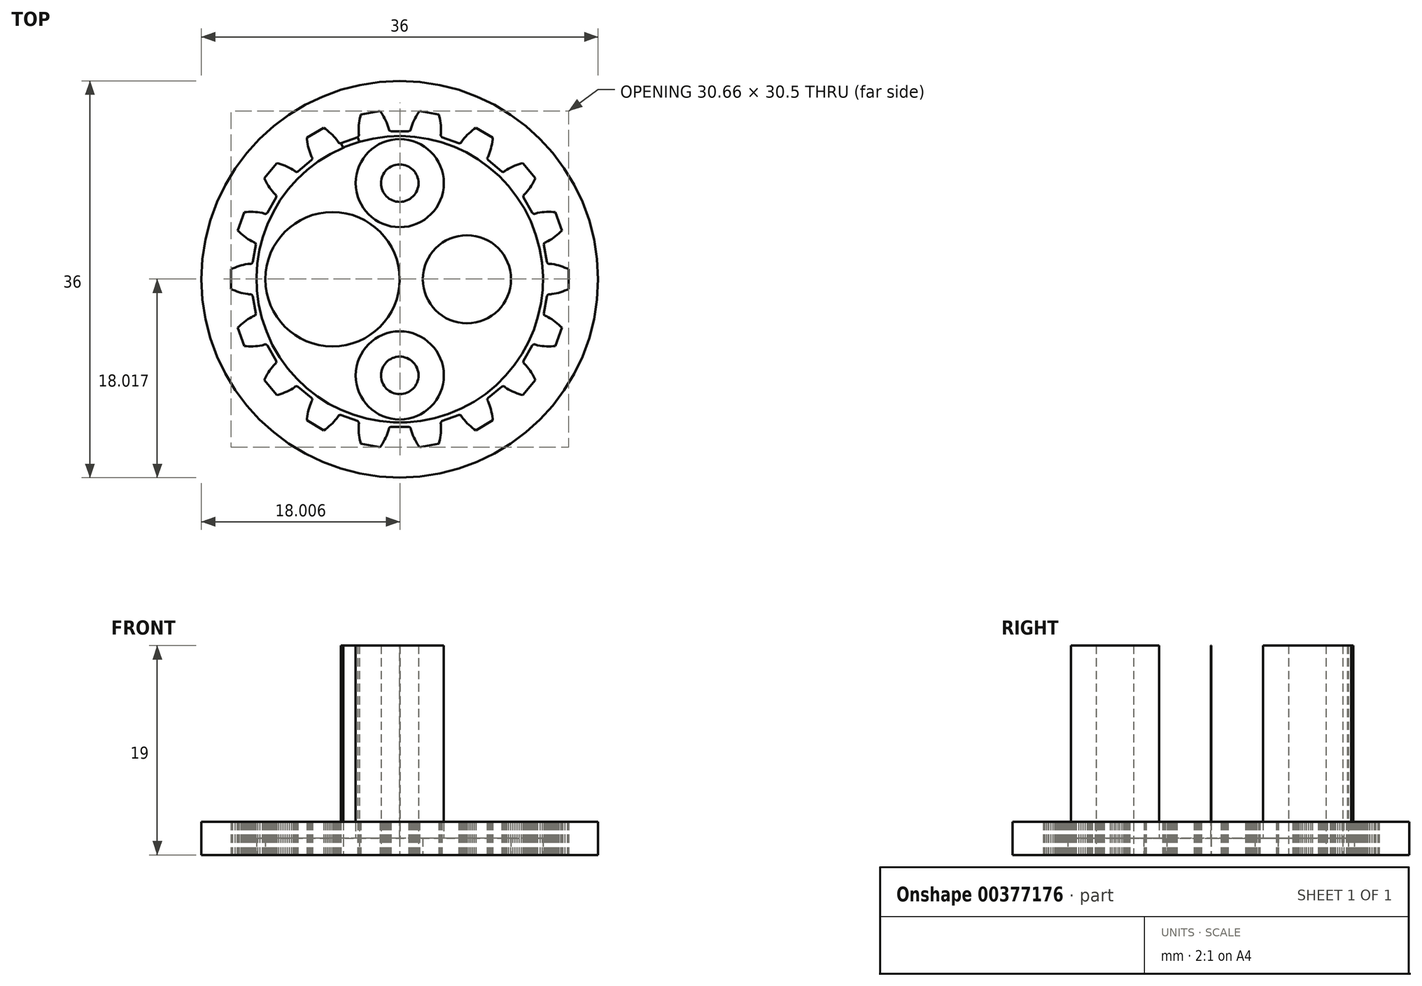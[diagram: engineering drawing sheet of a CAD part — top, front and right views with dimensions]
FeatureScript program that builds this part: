
annotation { "Feature Type Name" : "Feature", "Feature Type Description" : "" }
export const myFeature = defineFeature(function(context is Context, id is Id, definition is map)
    precondition{}
    {
        {
            var Q0;
            Q0=qCreatedBy(makeId("Top.planeOp"),FACE);
            var sketch = newSketch(context, id + "F0", { "sketchPlane" : qUnion([Q0])});
            skCircle(sketch, "E0", {"center": v(-6.1, 0) * mm, "radius": 6.1 * mm});
            skCircle(sketch, "E1.MirrorC", {"center": v(6.1, 0) * mm, "radius": 6.1 * mm});
            skCircle(sketch, "E2", {"center": v(0, 0) * mm, "radius": 18 * mm});
            skCircle(sketch, "E3", {"center": v(-6.1, 0) * mm, "radius": 4 * mm});
            skCircle(sketch, "E4", {"center": v(6.1, 0) * mm, "radius": 4 * mm});
            skCircle(sketch, "E5", {"center": v(0, -8.73) * mm, "radius": 4 * mm});
            skCircle(sketch, "E6", {"center": v(0, -8.73) * mm, "radius": 1.7 * mm});
            skCircle(sketch, "E7.cCircle", {"center": v(0, -8.73) * mm, "radius": 2.95 * mm, "construction": true});
            skLineSegment(sketch, "E7.0", {"start": v(0, -5.32) * mm, "end": v(2.95, -7.02) * mm});
            skLineSegment(sketch, "E7.1", {"start": v(2.95, -7.02) * mm, "end": v(2.95, -10.43) * mm});
            skLineSegment(sketch, "E7.2", {"start": v(2.95, -10.43) * mm, "end": v(0, -12.13) * mm});
            skLineSegment(sketch, "E7.3", {"start": v(0, -12.13) * mm, "end": v(-2.95, -10.43) * mm});
            skLineSegment(sketch, "E7.4", {"start": v(-2.95, -10.43) * mm, "end": v(-2.95, -7.02) * mm});
            skLineSegment(sketch, "E7.5", {"start": v(-2.95, -7.02) * mm, "end": v(0, -5.32) * mm});
            skLineSegment(sketch, "E8.MirrorCS", {"start": v(0, 12.13) * mm, "end": v(-2.95, 10.43) * mm});
            skLineSegment(sketch, "E9.MirrorCS", {"start": v(-2.95, 10.43) * mm, "end": v(-2.95, 7.02) * mm});
            skLineSegment(sketch, "E10.MirrorCS", {"start": v(-2.95, 7.02) * mm, "end": v(0, 5.32) * mm});
            skLineSegment(sketch, "E11.MirrorCS", {"start": v(2.95, 10.43) * mm, "end": v(0, 12.13) * mm});
            skCircle(sketch, "E12.MirrorC", {"center": v(0, 8.73) * mm, "radius": 1.7 * mm});
            skCircle(sketch, "E13.MirrorC", {"center": v(0, 8.73) * mm, "radius": 4 * mm});
            skLineSegment(sketch, "E14.MirrorCS", {"start": v(0, 5.32) * mm, "end": v(2.95, 7.02) * mm});
            skCircle(sketch, "E15.MirrorC", {"center": v(0, 8.73) * mm, "radius": 2.95 * mm, "construction": true});
            skLineSegment(sketch, "E16.MirrorCS", {"start": v(2.95, 7.02) * mm, "end": v(2.95, 10.43) * mm});
            skCircle(sketch, "E17", {"center": v(0, 0) * mm, "radius": 13 * mm});
            skLineSegment(sketch, "E18", {"start": v(13.36, 1.56) * mm, "end": v(13.42, 1.47) * mm});
            skLineSegment(sketch, "E19", {"start": v(13.42, 1.47) * mm, "end": v(13.48, 1.4) * mm});
            skLineSegment(sketch, "E20", {"start": v(13.48, 1.4) * mm, "end": v(13.52, 1.4) * mm});
            skLineSegment(sketch, "E21", {"start": v(13.52, 1.4) * mm, "end": v(13.62, 1.4) * mm});
            skLineSegment(sketch, "E22", {"start": v(13.62, 1.4) * mm, "end": v(13.72, 1.4) * mm});
            skLineSegment(sketch, "E23", {"start": v(13.72, 1.4) * mm, "end": v(13.81, 1.38) * mm});
            skLineSegment(sketch, "E24", {"start": v(13.81, 1.38) * mm, "end": v(14, 1.35) * mm});
            skLineSegment(sketch, "E25", {"start": v(14, 1.35) * mm, "end": v(14.2, 1.3) * mm});
            skLineSegment(sketch, "E26", {"start": v(14.2, 1.3) * mm, "end": v(14.4, 1.26) * mm});
            skLineSegment(sketch, "E27", {"start": v(14.4, 1.26) * mm, "end": v(14.6, 1.2) * mm});
            skLineSegment(sketch, "E28", {"start": v(14.6, 1.2) * mm, "end": v(14.8, 1.13) * mm});
            skLineSegment(sketch, "E29", {"start": v(14.8, 1.13) * mm, "end": v(15, 1.06) * mm});
            skLineSegment(sketch, "E30", {"start": v(15, 1.06) * mm, "end": v(15.19, 0.98) * mm});
            skLineSegment(sketch, "E31", {"start": v(15.19, 0.98) * mm, "end": v(15.33, 0.9) * mm});
            skLineSegment(sketch, "E32", {"start": v(15.33, 0.9) * mm, "end": v(15.33, -0.88) * mm});
            skLineSegment(sketch, "E33", {"start": v(15.33, -0.88) * mm, "end": v(15.19, -0.94) * mm});
            skLineSegment(sketch, "E34", {"start": v(15.19, -0.94) * mm, "end": v(15, -1.02) * mm});
            skLineSegment(sketch, "E35", {"start": v(15, -1.02) * mm, "end": v(14.8, -1.1) * mm});
            skLineSegment(sketch, "E36", {"start": v(14.8, -1.1) * mm, "end": v(14.6, -1.17) * mm});
            skLineSegment(sketch, "E37", {"start": v(14.6, -1.17) * mm, "end": v(14.4, -1.22) * mm});
            skLineSegment(sketch, "E38", {"start": v(14.4, -1.22) * mm, "end": v(14.2, -1.28) * mm});
            skLineSegment(sketch, "E39", {"start": v(14.2, -1.28) * mm, "end": v(14, -1.32) * mm});
            skLineSegment(sketch, "E40", {"start": v(14, -1.32) * mm, "end": v(13.81, -1.35) * mm});
            skLineSegment(sketch, "E41", {"start": v(13.81, -1.35) * mm, "end": v(13.72, -1.36) * mm});
            skLineSegment(sketch, "E42", {"start": v(13.72, -1.36) * mm, "end": v(13.62, -1.36) * mm});
            skLineSegment(sketch, "E43", {"start": v(13.62, -1.36) * mm, "end": v(13.52, -1.37) * mm});
            skLineSegment(sketch, "E44", {"start": v(13.52, -1.37) * mm, "end": v(13.48, -1.36) * mm});
            skLineSegment(sketch, "E45", {"start": v(13.48, -1.36) * mm, "end": v(13.42, -1.44) * mm});
            skLineSegment(sketch, "E46", {"start": v(13.42, -1.44) * mm, "end": v(13.36, -1.53) * mm});
            skLineSegment(sketch, "E47", {"start": v(13.36, -1.53) * mm, "end": v(13.08, -3.1) * mm});
            skLineSegment(sketch, "E48", {"start": v(13.08, -3.1) * mm, "end": v(13.1, -3.2) * mm});
            skLineSegment(sketch, "E49", {"start": v(13.1, -3.2) * mm, "end": v(13.14, -3.3) * mm});
            skLineSegment(sketch, "E50", {"start": v(13.14, -3.3) * mm, "end": v(13.18, -3.3) * mm});
            skLineSegment(sketch, "E51", {"start": v(13.18, -3.3) * mm, "end": v(13.27, -3.34) * mm});
            skLineSegment(sketch, "E52", {"start": v(13.27, -3.34) * mm, "end": v(13.36, -3.38) * mm});
            skLineSegment(sketch, "E53", {"start": v(13.36, -3.38) * mm, "end": v(13.45, -3.42) * mm});
            skLineSegment(sketch, "E54", {"start": v(13.45, -3.42) * mm, "end": v(13.62, -3.52) * mm});
            skLineSegment(sketch, "E55", {"start": v(13.62, -3.52) * mm, "end": v(13.79, -3.63) * mm});
            skLineSegment(sketch, "E56", {"start": v(13.79, -3.63) * mm, "end": v(13.96, -3.74) * mm});
            skLineSegment(sketch, "E57", {"start": v(13.96, -3.74) * mm, "end": v(14.12, -3.86) * mm});
            skLineSegment(sketch, "E58", {"start": v(14.12, -3.86) * mm, "end": v(14.28, -4) * mm});
            skLineSegment(sketch, "E59", {"start": v(14.28, -4) * mm, "end": v(14.44, -4.13) * mm});
            skLineSegment(sketch, "E60", {"start": v(14.44, -4.13) * mm, "end": v(14.6, -4.27) * mm});
            skLineSegment(sketch, "E61", {"start": v(14.6, -4.27) * mm, "end": v(14.72, -4.39) * mm});
            skLineSegment(sketch, "E62", {"start": v(14.72, -4.39) * mm, "end": v(14.1, -6.06) * mm});
            skLineSegment(sketch, "E63", {"start": v(14.1, -6.06) * mm, "end": v(13.94, -6.08) * mm});
            skLineSegment(sketch, "E64", {"start": v(13.94, -6.08) * mm, "end": v(13.73, -6.09) * mm});
            skLineSegment(sketch, "E65", {"start": v(13.73, -6.09) * mm, "end": v(13.52, -6.09) * mm});
            skLineSegment(sketch, "E66", {"start": v(13.52, -6.09) * mm, "end": v(13.31, -6.09) * mm});
            skLineSegment(sketch, "E67", {"start": v(13.31, -6.09) * mm, "end": v(13.1, -6.07) * mm});
            skLineSegment(sketch, "E68", {"start": v(13.1, -6.07) * mm, "end": v(12.9, -6.05) * mm});
            skLineSegment(sketch, "E69", {"start": v(12.9, -6.05) * mm, "end": v(12.7, -6.02) * mm});
            skLineSegment(sketch, "E70", {"start": v(12.7, -6.02) * mm, "end": v(12.51, -5.99) * mm});
            skLineSegment(sketch, "E71", {"start": v(12.51, -5.99) * mm, "end": v(12.42, -5.96) * mm});
            skLineSegment(sketch, "E72", {"start": v(12.42, -5.96) * mm, "end": v(12.33, -5.94) * mm});
            skLineSegment(sketch, "E73", {"start": v(12.33, -5.94) * mm, "end": v(12.24, -5.9) * mm});
            skLineSegment(sketch, "E74", {"start": v(12.24, -5.9) * mm, "end": v(12.2, -5.89) * mm});
            skLineSegment(sketch, "E75", {"start": v(12.2, -5.89) * mm, "end": v(12.11, -5.94) * mm});
            skLineSegment(sketch, "E76", {"start": v(12.11, -5.94) * mm, "end": v(12.03, -6) * mm});
            skLineSegment(sketch, "E77", {"start": v(12.03, -6) * mm, "end": v(11.23, -7.39) * mm});
            skLineSegment(sketch, "E78", {"start": v(11.23, -7.39) * mm, "end": v(11.22, -7.5) * mm});
            skLineSegment(sketch, "E79", {"start": v(11.22, -7.5) * mm, "end": v(11.21, -7.58) * mm});
            skLineSegment(sketch, "E80", {"start": v(11.21, -7.58) * mm, "end": v(11.25, -7.61) * mm});
            skLineSegment(sketch, "E81", {"start": v(11.25, -7.61) * mm, "end": v(11.32, -7.68) * mm});
            skLineSegment(sketch, "E82", {"start": v(11.32, -7.68) * mm, "end": v(11.4, -7.74) * mm});
            skLineSegment(sketch, "E83", {"start": v(11.4, -7.74) * mm, "end": v(11.46, -7.81) * mm});
            skLineSegment(sketch, "E84", {"start": v(11.46, -7.81) * mm, "end": v(11.59, -7.96) * mm});
            skLineSegment(sketch, "E85", {"start": v(11.59, -7.96) * mm, "end": v(11.71, -8.12) * mm});
            skLineSegment(sketch, "E86", {"start": v(11.71, -8.12) * mm, "end": v(11.83, -8.28) * mm});
            skLineSegment(sketch, "E87", {"start": v(11.83, -8.28) * mm, "end": v(11.94, -8.46) * mm});
            skLineSegment(sketch, "E88", {"start": v(11.94, -8.46) * mm, "end": v(12.05, -8.63) * mm});
            skLineSegment(sketch, "E89", {"start": v(12.05, -8.63) * mm, "end": v(12.15, -8.82) * mm});
            skLineSegment(sketch, "E90", {"start": v(12.15, -8.82) * mm, "end": v(12.25, -9) * mm});
            skLineSegment(sketch, "E91", {"start": v(12.25, -9) * mm, "end": v(12.32, -9.15) * mm});
            skLineSegment(sketch, "E92", {"start": v(12.32, -9.15) * mm, "end": v(11.17, -10.52) * mm});
            skLineSegment(sketch, "E93", {"start": v(11.17, -10.52) * mm, "end": v(11.02, -10.48) * mm});
            skLineSegment(sketch, "E94", {"start": v(11.02, -10.48) * mm, "end": v(10.82, -10.41) * mm});
            skLineSegment(sketch, "E95", {"start": v(10.82, -10.41) * mm, "end": v(10.62, -10.34) * mm});
            skLineSegment(sketch, "E96", {"start": v(10.62, -10.34) * mm, "end": v(10.42, -10.27) * mm});
            skLineSegment(sketch, "E97", {"start": v(10.42, -10.27) * mm, "end": v(10.23, -10.19) * mm});
            skLineSegment(sketch, "E98", {"start": v(10.23, -10.19) * mm, "end": v(10.05, -10.1) * mm});
            skLineSegment(sketch, "E99", {"start": v(10.05, -10.1) * mm, "end": v(9.88, -10) * mm});
            skLineSegment(sketch, "E100", {"start": v(9.88, -10) * mm, "end": v(9.7, -9.9) * mm});
            skLineSegment(sketch, "E101", {"start": v(9.7, -9.9) * mm, "end": v(9.63, -9.85) * mm});
            skLineSegment(sketch, "E102", {"start": v(9.63, -9.85) * mm, "end": v(9.55, -9.8) * mm});
            skLineSegment(sketch, "E103", {"start": v(9.55, -9.8) * mm, "end": v(9.47, -9.73) * mm});
            skLineSegment(sketch, "E104", {"start": v(9.47, -9.73) * mm, "end": v(9.44, -9.7) * mm});
            skLineSegment(sketch, "E105", {"start": v(9.44, -9.7) * mm, "end": v(9.35, -9.72) * mm});
            skLineSegment(sketch, "E106", {"start": v(9.35, -9.72) * mm, "end": v(9.25, -9.75) * mm});
            skLineSegment(sketch, "E107", {"start": v(9.25, -9.75) * mm, "end": v(8.02, -10.78) * mm});
            skLineSegment(sketch, "E108", {"start": v(8.02, -10.78) * mm, "end": v(7.97, -10.87) * mm});
            skLineSegment(sketch, "E109", {"start": v(7.97, -10.87) * mm, "end": v(7.94, -10.96) * mm});
            skLineSegment(sketch, "E110", {"start": v(7.94, -10.96) * mm, "end": v(7.96, -11) * mm});
            skLineSegment(sketch, "E111", {"start": v(7.96, -11) * mm, "end": v(8, -11.08) * mm});
            skLineSegment(sketch, "E112", {"start": v(8, -11.08) * mm, "end": v(8.05, -11.17) * mm});
            skLineSegment(sketch, "E113", {"start": v(8.05, -11.17) * mm, "end": v(8.1, -11.26) * mm});
            skLineSegment(sketch, "E114", {"start": v(8.1, -11.26) * mm, "end": v(8.16, -11.44) * mm});
            skLineSegment(sketch, "E115", {"start": v(8.16, -11.44) * mm, "end": v(8.22, -11.63) * mm});
            skLineSegment(sketch, "E116", {"start": v(8.22, -11.63) * mm, "end": v(8.28, -11.83) * mm});
            skLineSegment(sketch, "E117", {"start": v(8.28, -11.83) * mm, "end": v(8.33, -12.03) * mm});
            skLineSegment(sketch, "E118", {"start": v(8.33, -12.03) * mm, "end": v(8.37, -12.23) * mm});
            skLineSegment(sketch, "E119", {"start": v(8.37, -12.23) * mm, "end": v(8.4, -12.44) * mm});
            skLineSegment(sketch, "E120", {"start": v(8.4, -12.44) * mm, "end": v(8.43, -12.65) * mm});
            skLineSegment(sketch, "E121", {"start": v(8.43, -12.65) * mm, "end": v(8.44, -12.81) * mm});
            skLineSegment(sketch, "E122", {"start": v(8.44, -12.81) * mm, "end": v(6.9, -13.7) * mm});
            skLineSegment(sketch, "E123", {"start": v(6.9, -13.7) * mm, "end": v(6.77, -13.6) * mm});
            skLineSegment(sketch, "E124", {"start": v(6.77, -13.6) * mm, "end": v(6.6, -13.48) * mm});
            skLineSegment(sketch, "E125", {"start": v(6.6, -13.48) * mm, "end": v(6.43, -13.35) * mm});
            skLineSegment(sketch, "E126", {"start": v(6.43, -13.35) * mm, "end": v(6.28, -13.21) * mm});
            skLineSegment(sketch, "E127", {"start": v(6.28, -13.21) * mm, "end": v(6.13, -13.07) * mm});
            skLineSegment(sketch, "E128", {"start": v(6.13, -13.07) * mm, "end": v(5.99, -12.93) * mm});
            skLineSegment(sketch, "E129", {"start": v(5.99, -12.93) * mm, "end": v(5.85, -12.78) * mm});
            skLineSegment(sketch, "E130", {"start": v(5.85, -12.78) * mm, "end": v(5.73, -12.62) * mm});
            skLineSegment(sketch, "E131", {"start": v(5.73, -12.62) * mm, "end": v(5.67, -12.54) * mm});
            skLineSegment(sketch, "E132", {"start": v(5.67, -12.54) * mm, "end": v(5.62, -12.46) * mm});
            skLineSegment(sketch, "E133", {"start": v(5.62, -12.46) * mm, "end": v(5.57, -12.38) * mm});
            skLineSegment(sketch, "E134", {"start": v(5.57, -12.38) * mm, "end": v(5.55, -12.34) * mm});
            skLineSegment(sketch, "E135", {"start": v(5.55, -12.34) * mm, "end": v(5.45, -12.33) * mm});
            skLineSegment(sketch, "E136", {"start": v(5.45, -12.33) * mm, "end": v(5.35, -12.32) * mm});
            skLineSegment(sketch, "E137", {"start": v(5.35, -12.32) * mm, "end": v(3.84, -12.87) * mm});
            skLineSegment(sketch, "E138", {"start": v(3.84, -12.87) * mm, "end": v(3.77, -12.94) * mm});
            skLineSegment(sketch, "E139", {"start": v(3.77, -12.94) * mm, "end": v(3.7, -13) * mm});
            skLineSegment(sketch, "E140", {"start": v(3.7, -13) * mm, "end": v(3.71, -13.06) * mm});
            skLineSegment(sketch, "E141", {"start": v(3.71, -13.06) * mm, "end": v(3.73, -13.15) * mm});
            skLineSegment(sketch, "E142", {"start": v(3.73, -13.15) * mm, "end": v(3.74, -13.25) * mm});
            skLineSegment(sketch, "E143", {"start": v(3.74, -13.25) * mm, "end": v(3.75, -13.34) * mm});
            skLineSegment(sketch, "E144", {"start": v(3.75, -13.34) * mm, "end": v(3.75, -13.54) * mm});
            skLineSegment(sketch, "E145", {"start": v(3.75, -13.54) * mm, "end": v(3.74, -13.74) * mm});
            skLineSegment(sketch, "E146", {"start": v(3.74, -13.74) * mm, "end": v(3.73, -13.94) * mm});
            skLineSegment(sketch, "E147", {"start": v(3.73, -13.94) * mm, "end": v(3.7, -14.15) * mm});
            skLineSegment(sketch, "E148", {"start": v(3.7, -14.15) * mm, "end": v(3.67, -14.35) * mm});
            skLineSegment(sketch, "E149", {"start": v(3.67, -14.35) * mm, "end": v(3.63, -14.56) * mm});
            skLineSegment(sketch, "E150", {"start": v(3.63, -14.56) * mm, "end": v(3.59, -14.77) * mm});
            skLineSegment(sketch, "E151", {"start": v(3.59, -14.77) * mm, "end": v(3.55, -14.92) * mm});
            skLineSegment(sketch, "E152", {"start": v(3.55, -14.92) * mm, "end": v(1.79, -15.23) * mm});
            skLineSegment(sketch, "E153", {"start": v(1.79, -15.23) * mm, "end": v(1.7, -15.1) * mm});
            skLineSegment(sketch, "E154", {"start": v(1.7, -15.1) * mm, "end": v(1.58, -14.92) * mm});
            skLineSegment(sketch, "E155", {"start": v(1.58, -14.92) * mm, "end": v(1.48, -14.74) * mm});
            skLineSegment(sketch, "E156", {"start": v(1.48, -14.74) * mm, "end": v(1.37, -14.56) * mm});
            skLineSegment(sketch, "E157", {"start": v(1.37, -14.56) * mm, "end": v(1.28, -14.37) * mm});
            skLineSegment(sketch, "E158", {"start": v(1.28, -14.37) * mm, "end": v(1.2, -14.2) * mm});
            skLineSegment(sketch, "E159", {"start": v(1.2, -14.2) * mm, "end": v(1.12, -14) * mm});
            skLineSegment(sketch, "E160", {"start": v(1.12, -14) * mm, "end": v(1.06, -13.82) * mm});
            skLineSegment(sketch, "E161", {"start": v(1.06, -13.82) * mm, "end": v(1.03, -13.72) * mm});
            skLineSegment(sketch, "E162", {"start": v(1.03, -13.72) * mm, "end": v(1.01, -13.63) * mm});
            skLineSegment(sketch, "E163", {"start": v(1.01, -13.63) * mm, "end": v(1, -13.54) * mm});
            skLineSegment(sketch, "E164", {"start": v(1, -13.54) * mm, "end": v(0.99, -13.49) * mm});
            skLineSegment(sketch, "E165", {"start": v(0.99, -13.49) * mm, "end": v(0.9, -13.45) * mm});
            skLineSegment(sketch, "E166", {"start": v(0.9, -13.45) * mm, "end": v(0.8, -13.4) * mm});
            skLineSegment(sketch, "E167", {"start": v(0.8, -13.4) * mm, "end": v(-0.8, -13.4) * mm});
            skLineSegment(sketch, "E168", {"start": v(-0.8, -13.4) * mm, "end": v(-0.9, -13.45) * mm});
            skLineSegment(sketch, "E169", {"start": v(-0.9, -13.45) * mm, "end": v(-0.97, -13.49) * mm});
            skLineSegment(sketch, "E170", {"start": v(-0.97, -13.49) * mm, "end": v(-0.98, -13.54) * mm});
            skLineSegment(sketch, "E171", {"start": v(-0.98, -13.54) * mm, "end": v(-1, -13.63) * mm});
            skLineSegment(sketch, "E172", {"start": v(-1, -13.63) * mm, "end": v(-1.02, -13.72) * mm});
            skLineSegment(sketch, "E173", {"start": v(-1.02, -13.72) * mm, "end": v(-1.05, -13.82) * mm});
            skLineSegment(sketch, "E174", {"start": v(-1.05, -13.82) * mm, "end": v(-1.11, -14) * mm});
            skLineSegment(sketch, "E175", {"start": v(-1.11, -14) * mm, "end": v(-1.19, -14.2) * mm});
            skLineSegment(sketch, "E176", {"start": v(-1.19, -14.2) * mm, "end": v(-1.27, -14.37) * mm});
            skLineSegment(sketch, "E177", {"start": v(-1.27, -14.37) * mm, "end": v(-1.36, -14.56) * mm});
            skLineSegment(sketch, "E178", {"start": v(-1.36, -14.56) * mm, "end": v(-1.46, -14.74) * mm});
            skLineSegment(sketch, "E179", {"start": v(-1.46, -14.74) * mm, "end": v(-1.57, -14.92) * mm});
            skLineSegment(sketch, "E180", {"start": v(-1.57, -14.92) * mm, "end": v(-1.69, -15.1) * mm});
            skLineSegment(sketch, "E181", {"start": v(-1.69, -15.1) * mm, "end": v(-1.78, -15.23) * mm});
            skLineSegment(sketch, "E182", {"start": v(-1.78, -15.23) * mm, "end": v(-3.53, -14.92) * mm});
            skLineSegment(sketch, "E183", {"start": v(-3.53, -14.92) * mm, "end": v(-3.57, -14.77) * mm});
            skLineSegment(sketch, "E184", {"start": v(-3.57, -14.77) * mm, "end": v(-3.62, -14.56) * mm});
            skLineSegment(sketch, "E185", {"start": v(-3.62, -14.56) * mm, "end": v(-3.66, -14.35) * mm});
            skLineSegment(sketch, "E186", {"start": v(-3.66, -14.35) * mm, "end": v(-3.7, -14.15) * mm});
            skLineSegment(sketch, "E187", {"start": v(-3.7, -14.15) * mm, "end": v(-3.72, -13.94) * mm});
            skLineSegment(sketch, "E188", {"start": v(-3.72, -13.94) * mm, "end": v(-3.73, -13.74) * mm});
            skLineSegment(sketch, "E189", {"start": v(-3.73, -13.74) * mm, "end": v(-3.74, -13.54) * mm});
            skLineSegment(sketch, "E190", {"start": v(-3.74, -13.54) * mm, "end": v(-3.73, -13.34) * mm});
            skLineSegment(sketch, "E191", {"start": v(-3.73, -13.34) * mm, "end": v(-3.73, -13.25) * mm});
            skLineSegment(sketch, "E192", {"start": v(-3.73, -13.25) * mm, "end": v(-3.72, -13.15) * mm});
            skLineSegment(sketch, "E193", {"start": v(-3.72, -13.15) * mm, "end": v(-3.7, -13.06) * mm});
            skLineSegment(sketch, "E194", {"start": v(-3.7, -13.06) * mm, "end": v(-3.7, -13) * mm});
            skLineSegment(sketch, "E195", {"start": v(-3.7, -13) * mm, "end": v(-3.76, -12.94) * mm});
            skLineSegment(sketch, "E196", {"start": v(-3.76, -12.94) * mm, "end": v(-3.83, -12.87) * mm});
            skLineSegment(sketch, "E197", {"start": v(-3.83, -12.87) * mm, "end": v(-5.34, -12.32) * mm});
            skLineSegment(sketch, "E198", {"start": v(-5.34, -12.32) * mm, "end": v(-5.44, -12.33) * mm});
            skLineSegment(sketch, "E199", {"start": v(-5.44, -12.33) * mm, "end": v(-5.53, -12.34) * mm});
            skLineSegment(sketch, "E200", {"start": v(-5.53, -12.34) * mm, "end": v(-5.56, -12.38) * mm});
            skLineSegment(sketch, "E201", {"start": v(-5.56, -12.38) * mm, "end": v(-5.6, -12.46) * mm});
            skLineSegment(sketch, "E202", {"start": v(-5.6, -12.46) * mm, "end": v(-5.66, -12.54) * mm});
            skLineSegment(sketch, "E203", {"start": v(-5.66, -12.54) * mm, "end": v(-5.72, -12.62) * mm});
            skLineSegment(sketch, "E204", {"start": v(-5.72, -12.62) * mm, "end": v(-5.84, -12.78) * mm});
            skLineSegment(sketch, "E205", {"start": v(-5.84, -12.78) * mm, "end": v(-5.97, -12.93) * mm});
            skLineSegment(sketch, "E206", {"start": v(-5.97, -12.93) * mm, "end": v(-6.12, -13.07) * mm});
            skLineSegment(sketch, "E207", {"start": v(-6.12, -13.07) * mm, "end": v(-6.27, -13.21) * mm});
            skLineSegment(sketch, "E208", {"start": v(-6.27, -13.21) * mm, "end": v(-6.42, -13.35) * mm});
            skLineSegment(sketch, "E209", {"start": v(-6.42, -13.35) * mm, "end": v(-6.59, -13.48) * mm});
            skLineSegment(sketch, "E210", {"start": v(-6.59, -13.48) * mm, "end": v(-6.75, -13.6) * mm});
            skLineSegment(sketch, "E211", {"start": v(-6.75, -13.6) * mm, "end": v(-6.89, -13.7) * mm});
            skLineSegment(sketch, "E212", {"start": v(-6.89, -13.7) * mm, "end": v(-8.43, -12.81) * mm});
            skLineSegment(sketch, "E213", {"start": v(-8.43, -12.81) * mm, "end": v(-8.41, -12.65) * mm});
            skLineSegment(sketch, "E214", {"start": v(-8.41, -12.65) * mm, "end": v(-8.39, -12.44) * mm});
            skLineSegment(sketch, "E215", {"start": v(-8.39, -12.44) * mm, "end": v(-8.35, -12.23) * mm});
            skLineSegment(sketch, "E216", {"start": v(-8.35, -12.23) * mm, "end": v(-8.31, -12.03) * mm});
            skLineSegment(sketch, "E217", {"start": v(-8.31, -12.03) * mm, "end": v(-8.27, -11.83) * mm});
            skLineSegment(sketch, "E218", {"start": v(-8.27, -11.83) * mm, "end": v(-8.21, -11.63) * mm});
            skLineSegment(sketch, "E219", {"start": v(-8.21, -11.63) * mm, "end": v(-8.15, -11.44) * mm});
            skLineSegment(sketch, "E220", {"start": v(-8.15, -11.44) * mm, "end": v(-8.08, -11.26) * mm});
            skLineSegment(sketch, "E221", {"start": v(-8.08, -11.26) * mm, "end": v(-8.04, -11.17) * mm});
            skLineSegment(sketch, "E222", {"start": v(-8.04, -11.17) * mm, "end": v(-8, -11.08) * mm});
            skLineSegment(sketch, "E223", {"start": v(-8, -11.08) * mm, "end": v(-7.95, -11) * mm});
            skLineSegment(sketch, "E224", {"start": v(-7.95, -11) * mm, "end": v(-7.93, -10.96) * mm});
            skLineSegment(sketch, "E225", {"start": v(-7.93, -10.96) * mm, "end": v(-7.96, -10.87) * mm});
            skLineSegment(sketch, "E226", {"start": v(-7.96, -10.87) * mm, "end": v(-8, -10.78) * mm});
            skLineSegment(sketch, "E227", {"start": v(-8, -10.78) * mm, "end": v(-9.24, -9.75) * mm});
            skLineSegment(sketch, "E228", {"start": v(-9.24, -9.75) * mm, "end": v(-9.33, -9.72) * mm});
            skLineSegment(sketch, "E229", {"start": v(-9.33, -9.72) * mm, "end": v(-9.43, -9.7) * mm});
            skLineSegment(sketch, "E230", {"start": v(-9.43, -9.7) * mm, "end": v(-9.46, -9.73) * mm});
            skLineSegment(sketch, "E231", {"start": v(-9.46, -9.73) * mm, "end": v(-9.54, -9.8) * mm});
            skLineSegment(sketch, "E232", {"start": v(-9.54, -9.8) * mm, "end": v(-9.61, -9.85) * mm});
            skLineSegment(sketch, "E233", {"start": v(-9.61, -9.85) * mm, "end": v(-9.7, -9.9) * mm});
            skLineSegment(sketch, "E234", {"start": v(-9.7, -9.9) * mm, "end": v(-9.86, -10) * mm});
            skLineSegment(sketch, "E235", {"start": v(-9.86, -10) * mm, "end": v(-10.04, -10.1) * mm});
            skLineSegment(sketch, "E236", {"start": v(-10.04, -10.1) * mm, "end": v(-10.22, -10.19) * mm});
            skLineSegment(sketch, "E237", {"start": v(-10.22, -10.19) * mm, "end": v(-10.41, -10.27) * mm});
            skLineSegment(sketch, "E238", {"start": v(-10.41, -10.27) * mm, "end": v(-10.6, -10.34) * mm});
            skLineSegment(sketch, "E239", {"start": v(-10.6, -10.34) * mm, "end": v(-10.8, -10.41) * mm});
            skLineSegment(sketch, "E240", {"start": v(-10.8, -10.41) * mm, "end": v(-11, -10.48) * mm});
            skLineSegment(sketch, "E241", {"start": v(-11, -10.48) * mm, "end": v(-11.16, -10.52) * mm});
            skLineSegment(sketch, "E242", {"start": v(-11.16, -10.52) * mm, "end": v(-12.31, -9.15) * mm});
            skLineSegment(sketch, "E243", {"start": v(-12.31, -9.15) * mm, "end": v(-12.24, -9) * mm});
            skLineSegment(sketch, "E244", {"start": v(-12.24, -9) * mm, "end": v(-12.14, -8.82) * mm});
            skLineSegment(sketch, "E245", {"start": v(-12.14, -8.82) * mm, "end": v(-12.04, -8.63) * mm});
            skLineSegment(sketch, "E246", {"start": v(-12.04, -8.63) * mm, "end": v(-11.93, -8.46) * mm});
            skLineSegment(sketch, "E247", {"start": v(-11.93, -8.46) * mm, "end": v(-11.82, -8.28) * mm});
            skLineSegment(sketch, "E248", {"start": v(-11.82, -8.28) * mm, "end": v(-11.7, -8.12) * mm});
            skLineSegment(sketch, "E249", {"start": v(-11.7, -8.12) * mm, "end": v(-11.58, -7.96) * mm});
            skLineSegment(sketch, "E250", {"start": v(-11.58, -7.96) * mm, "end": v(-11.45, -7.81) * mm});
            skLineSegment(sketch, "E251", {"start": v(-11.45, -7.81) * mm, "end": v(-11.38, -7.74) * mm});
            skLineSegment(sketch, "E252", {"start": v(-11.38, -7.74) * mm, "end": v(-11.31, -7.68) * mm});
            skLineSegment(sketch, "E253", {"start": v(-11.31, -7.68) * mm, "end": v(-11.24, -7.61) * mm});
            skLineSegment(sketch, "E254", {"start": v(-11.24, -7.61) * mm, "end": v(-11.2, -7.58) * mm});
            skLineSegment(sketch, "E255", {"start": v(-11.2, -7.58) * mm, "end": v(-11.2, -7.5) * mm});
            skLineSegment(sketch, "E256", {"start": v(-11.2, -7.5) * mm, "end": v(-11.22, -7.39) * mm});
            skLineSegment(sketch, "E257", {"start": v(-11.22, -7.39) * mm, "end": v(-12.02, -6) * mm});
            skLineSegment(sketch, "E258", {"start": v(-12.02, -6) * mm, "end": v(-12.1, -5.94) * mm});
            skLineSegment(sketch, "E259", {"start": v(-12.1, -5.94) * mm, "end": v(-12.18, -5.89) * mm});
            skLineSegment(sketch, "E260", {"start": v(-12.18, -5.89) * mm, "end": v(-12.22, -5.9) * mm});
            skLineSegment(sketch, "E261", {"start": v(-12.22, -5.9) * mm, "end": v(-12.32, -5.94) * mm});
            skLineSegment(sketch, "E262", {"start": v(-12.32, -5.94) * mm, "end": v(-12.4, -5.96) * mm});
            skLineSegment(sketch, "E263", {"start": v(-12.4, -5.96) * mm, "end": v(-12.5, -5.99) * mm});
            skLineSegment(sketch, "E264", {"start": v(-12.5, -5.99) * mm, "end": v(-12.7, -6.02) * mm});
            skLineSegment(sketch, "E265", {"start": v(-12.7, -6.02) * mm, "end": v(-12.9, -6.05) * mm});
            skLineSegment(sketch, "E266", {"start": v(-12.9, -6.05) * mm, "end": v(-13.1, -6.07) * mm});
            skLineSegment(sketch, "E267", {"start": v(-13.1, -6.07) * mm, "end": v(-13.3, -6.09) * mm});
            skLineSegment(sketch, "E268", {"start": v(-13.3, -6.09) * mm, "end": v(-13.5, -6.09) * mm});
            skLineSegment(sketch, "E269", {"start": v(-13.5, -6.09) * mm, "end": v(-13.72, -6.09) * mm});
            skLineSegment(sketch, "E270", {"start": v(-13.72, -6.09) * mm, "end": v(-13.93, -6.08) * mm});
            skLineSegment(sketch, "E271", {"start": v(-13.93, -6.08) * mm, "end": v(-14.1, -6.06) * mm});
            skLineSegment(sketch, "E272", {"start": v(-14.1, -6.06) * mm, "end": v(-14.7, -4.39) * mm});
            skLineSegment(sketch, "E273", {"start": v(-14.7, -4.39) * mm, "end": v(-14.59, -4.27) * mm});
            skLineSegment(sketch, "E274", {"start": v(-14.59, -4.27) * mm, "end": v(-14.43, -4.13) * mm});
            skLineSegment(sketch, "E275", {"start": v(-14.43, -4.13) * mm, "end": v(-14.27, -4) * mm});
            skLineSegment(sketch, "E276", {"start": v(-14.27, -4) * mm, "end": v(-14.1, -3.86) * mm});
            skLineSegment(sketch, "E277", {"start": v(-14.1, -3.86) * mm, "end": v(-13.95, -3.74) * mm});
            skLineSegment(sketch, "E278", {"start": v(-13.95, -3.74) * mm, "end": v(-13.78, -3.63) * mm});
            skLineSegment(sketch, "E279", {"start": v(-13.78, -3.63) * mm, "end": v(-13.6, -3.52) * mm});
            skLineSegment(sketch, "E280", {"start": v(-13.6, -3.52) * mm, "end": v(-13.44, -3.42) * mm});
            skLineSegment(sketch, "E281", {"start": v(-13.44, -3.42) * mm, "end": v(-13.35, -3.38) * mm});
            skLineSegment(sketch, "E282", {"start": v(-13.35, -3.38) * mm, "end": v(-13.26, -3.34) * mm});
            skLineSegment(sketch, "E283", {"start": v(-13.26, -3.34) * mm, "end": v(-13.17, -3.3) * mm});
            skLineSegment(sketch, "E284", {"start": v(-13.17, -3.3) * mm, "end": v(-13.12, -3.3) * mm});
            skLineSegment(sketch, "E285", {"start": v(-13.12, -3.3) * mm, "end": v(-13.1, -3.2) * mm});
            skLineSegment(sketch, "E286", {"start": v(-13.1, -3.2) * mm, "end": v(-13.07, -3.1) * mm});
            skLineSegment(sketch, "E287", {"start": v(-13.07, -3.1) * mm, "end": v(-13.35, -1.53) * mm});
            skLineSegment(sketch, "E288", {"start": v(-13.35, -1.53) * mm, "end": v(-13.4, -1.44) * mm});
            skLineSegment(sketch, "E289", {"start": v(-13.4, -1.44) * mm, "end": v(-13.46, -1.36) * mm});
            skLineSegment(sketch, "E290", {"start": v(-13.46, -1.36) * mm, "end": v(-13.51, -1.37) * mm});
            skLineSegment(sketch, "E291", {"start": v(-13.51, -1.37) * mm, "end": v(-13.6, -1.36) * mm});
            skLineSegment(sketch, "E292", {"start": v(-13.6, -1.36) * mm, "end": v(-13.7, -1.36) * mm});
            skLineSegment(sketch, "E293", {"start": v(-13.7, -1.36) * mm, "end": v(-13.8, -1.35) * mm});
            skLineSegment(sketch, "E294", {"start": v(-13.8, -1.35) * mm, "end": v(-14, -1.32) * mm});
            skLineSegment(sketch, "E295", {"start": v(-14, -1.32) * mm, "end": v(-14.2, -1.28) * mm});
            skLineSegment(sketch, "E296", {"start": v(-14.2, -1.28) * mm, "end": v(-14.39, -1.22) * mm});
            skLineSegment(sketch, "E297", {"start": v(-14.39, -1.22) * mm, "end": v(-14.58, -1.17) * mm});
            skLineSegment(sketch, "E298", {"start": v(-14.58, -1.17) * mm, "end": v(-14.78, -1.1) * mm});
            skLineSegment(sketch, "E299", {"start": v(-14.78, -1.1) * mm, "end": v(-14.98, -1.02) * mm});
            skLineSegment(sketch, "E300", {"start": v(-14.98, -1.02) * mm, "end": v(-15.18, -0.94) * mm});
            skLineSegment(sketch, "E301", {"start": v(-15.18, -0.94) * mm, "end": v(-15.32, -0.88) * mm});
            skLineSegment(sketch, "E302", {"start": v(-15.32, -0.88) * mm, "end": v(-15.32, 0.9) * mm});
            skLineSegment(sketch, "E303", {"start": v(-15.32, 0.9) * mm, "end": v(-15.18, 0.98) * mm});
            skLineSegment(sketch, "E304", {"start": v(-15.18, 0.98) * mm, "end": v(-14.98, 1.06) * mm});
            skLineSegment(sketch, "E305", {"start": v(-14.98, 1.06) * mm, "end": v(-14.78, 1.13) * mm});
            skLineSegment(sketch, "E306", {"start": v(-14.78, 1.13) * mm, "end": v(-14.58, 1.2) * mm});
            skLineSegment(sketch, "E307", {"start": v(-14.58, 1.2) * mm, "end": v(-14.39, 1.26) * mm});
            skLineSegment(sketch, "E308", {"start": v(-14.39, 1.26) * mm, "end": v(-14.2, 1.3) * mm});
            skLineSegment(sketch, "E309", {"start": v(-14.2, 1.3) * mm, "end": v(-14, 1.35) * mm});
            skLineSegment(sketch, "E310", {"start": v(-14, 1.35) * mm, "end": v(-13.8, 1.38) * mm});
            skLineSegment(sketch, "E311", {"start": v(-13.8, 1.38) * mm, "end": v(-13.7, 1.4) * mm});
            skLineSegment(sketch, "E312", {"start": v(-13.7, 1.4) * mm, "end": v(-13.6, 1.4) * mm});
            skLineSegment(sketch, "E313", {"start": v(-13.6, 1.4) * mm, "end": v(-13.51, 1.4) * mm});
            skLineSegment(sketch, "E314", {"start": v(-13.51, 1.4) * mm, "end": v(-13.46, 1.4) * mm});
            skLineSegment(sketch, "E315", {"start": v(-13.46, 1.4) * mm, "end": v(-13.4, 1.47) * mm});
            skLineSegment(sketch, "E316", {"start": v(-13.4, 1.47) * mm, "end": v(-13.35, 1.56) * mm});
            skLineSegment(sketch, "E317", {"start": v(-13.35, 1.56) * mm, "end": v(-13.07, 3.14) * mm});
            skLineSegment(sketch, "E318", {"start": v(-13.07, 3.14) * mm, "end": v(-13.1, 3.24) * mm});
            skLineSegment(sketch, "E319", {"start": v(-13.1, 3.24) * mm, "end": v(-13.12, 3.33) * mm});
            skLineSegment(sketch, "E320", {"start": v(-13.12, 3.33) * mm, "end": v(-13.17, 3.34) * mm});
            skLineSegment(sketch, "E321", {"start": v(-13.17, 3.34) * mm, "end": v(-13.26, 3.38) * mm});
            skLineSegment(sketch, "E322", {"start": v(-13.26, 3.38) * mm, "end": v(-13.35, 3.42) * mm});
            skLineSegment(sketch, "E323", {"start": v(-13.35, 3.42) * mm, "end": v(-13.44, 3.46) * mm});
            skLineSegment(sketch, "E324", {"start": v(-13.44, 3.46) * mm, "end": v(-13.6, 3.55) * mm});
            skLineSegment(sketch, "E325", {"start": v(-13.6, 3.55) * mm, "end": v(-13.78, 3.66) * mm});
            skLineSegment(sketch, "E326", {"start": v(-13.78, 3.66) * mm, "end": v(-13.95, 3.77) * mm});
            skLineSegment(sketch, "E327", {"start": v(-13.95, 3.77) * mm, "end": v(-14.1, 3.9) * mm});
            skLineSegment(sketch, "E328", {"start": v(-14.1, 3.9) * mm, "end": v(-14.27, 4.03) * mm});
            skLineSegment(sketch, "E329", {"start": v(-14.27, 4.03) * mm, "end": v(-14.43, 4.16) * mm});
            skLineSegment(sketch, "E330", {"start": v(-14.43, 4.16) * mm, "end": v(-14.59, 4.3) * mm});
            skLineSegment(sketch, "E331", {"start": v(-14.59, 4.3) * mm, "end": v(-14.7, 4.42) * mm});
            skLineSegment(sketch, "E332", {"start": v(-14.7, 4.42) * mm, "end": v(-14.1, 6.1) * mm});
            skLineSegment(sketch, "E333", {"start": v(-14.1, 6.1) * mm, "end": v(-13.93, 6.1) * mm});
            skLineSegment(sketch, "E334", {"start": v(-13.93, 6.1) * mm, "end": v(-13.72, 6.12) * mm});
            skLineSegment(sketch, "E335", {"start": v(-13.72, 6.12) * mm, "end": v(-13.5, 6.12) * mm});
            skLineSegment(sketch, "E336", {"start": v(-13.5, 6.12) * mm, "end": v(-13.3, 6.12) * mm});
            skLineSegment(sketch, "E337", {"start": v(-13.3, 6.12) * mm, "end": v(-13.1, 6.1) * mm});
            skLineSegment(sketch, "E338", {"start": v(-13.1, 6.1) * mm, "end": v(-12.9, 6.09) * mm});
            skLineSegment(sketch, "E339", {"start": v(-12.9, 6.09) * mm, "end": v(-12.7, 6.06) * mm});
            skLineSegment(sketch, "E340", {"start": v(-12.7, 6.06) * mm, "end": v(-12.5, 6.02) * mm});
            skLineSegment(sketch, "E341", {"start": v(-12.5, 6.02) * mm, "end": v(-12.4, 6) * mm});
            skLineSegment(sketch, "E342", {"start": v(-12.4, 6) * mm, "end": v(-12.32, 5.97) * mm});
            skLineSegment(sketch, "E343", {"start": v(-12.32, 5.97) * mm, "end": v(-12.22, 5.94) * mm});
            skLineSegment(sketch, "E344", {"start": v(-12.22, 5.94) * mm, "end": v(-12.18, 5.92) * mm});
            skLineSegment(sketch, "E345", {"start": v(-12.18, 5.92) * mm, "end": v(-12.1, 5.97) * mm});
            skLineSegment(sketch, "E346", {"start": v(-12.1, 5.97) * mm, "end": v(-12.02, 6.03) * mm});
            skLineSegment(sketch, "E347", {"start": v(-12.02, 6.03) * mm, "end": v(-11.22, 7.42) * mm});
            skLineSegment(sketch, "E348", {"start": v(-11.22, 7.42) * mm, "end": v(-11.2, 7.52) * mm});
            skLineSegment(sketch, "E349", {"start": v(-11.2, 7.52) * mm, "end": v(-11.2, 7.62) * mm});
            skLineSegment(sketch, "E350", {"start": v(-11.2, 7.62) * mm, "end": v(-11.24, 7.65) * mm});
            skLineSegment(sketch, "E351", {"start": v(-11.24, 7.65) * mm, "end": v(-11.31, 7.71) * mm});
            skLineSegment(sketch, "E352", {"start": v(-11.31, 7.71) * mm, "end": v(-11.38, 7.78) * mm});
            skLineSegment(sketch, "E353", {"start": v(-11.38, 7.78) * mm, "end": v(-11.45, 7.85) * mm});
            skLineSegment(sketch, "E354", {"start": v(-11.45, 7.85) * mm, "end": v(-11.58, 8) * mm});
            skLineSegment(sketch, "E355", {"start": v(-11.58, 8) * mm, "end": v(-11.7, 8.15) * mm});
            skLineSegment(sketch, "E356", {"start": v(-11.7, 8.15) * mm, "end": v(-11.82, 8.32) * mm});
            skLineSegment(sketch, "E357", {"start": v(-11.82, 8.32) * mm, "end": v(-11.93, 8.49) * mm});
            skLineSegment(sketch, "E358", {"start": v(-11.93, 8.49) * mm, "end": v(-12.04, 8.67) * mm});
            skLineSegment(sketch, "E359", {"start": v(-12.04, 8.67) * mm, "end": v(-12.14, 8.85) * mm});
            skLineSegment(sketch, "E360", {"start": v(-12.14, 8.85) * mm, "end": v(-12.24, 9.04) * mm});
            skLineSegment(sketch, "E361", {"start": v(-12.24, 9.04) * mm, "end": v(-12.31, 9.19) * mm});
            skLineSegment(sketch, "E362", {"start": v(-12.31, 9.19) * mm, "end": v(-11.16, 10.55) * mm});
            skLineSegment(sketch, "E363", {"start": v(-11.16, 10.55) * mm, "end": v(-11, 10.5) * mm});
            skLineSegment(sketch, "E364", {"start": v(-11, 10.5) * mm, "end": v(-10.8, 10.45) * mm});
            skLineSegment(sketch, "E365", {"start": v(-10.8, 10.45) * mm, "end": v(-10.6, 10.38) * mm});
            skLineSegment(sketch, "E366", {"start": v(-10.6, 10.38) * mm, "end": v(-10.41, 10.3) * mm});
            skLineSegment(sketch, "E367", {"start": v(-10.41, 10.3) * mm, "end": v(-10.22, 10.22) * mm});
            skLineSegment(sketch, "E368", {"start": v(-10.22, 10.22) * mm, "end": v(-10.04, 10.13) * mm});
            skLineSegment(sketch, "E369", {"start": v(-10.04, 10.13) * mm, "end": v(-9.86, 10.04) * mm});
            skLineSegment(sketch, "E370", {"start": v(-9.86, 10.04) * mm, "end": v(-9.7, 9.94) * mm});
            skLineSegment(sketch, "E371", {"start": v(-9.7, 9.94) * mm, "end": v(-9.61, 9.88) * mm});
            skLineSegment(sketch, "E372", {"start": v(-9.61, 9.88) * mm, "end": v(-9.54, 9.83) * mm});
            skLineSegment(sketch, "E373", {"start": v(-9.54, 9.83) * mm, "end": v(-9.46, 9.76) * mm});
            skLineSegment(sketch, "E374", {"start": v(-9.46, 9.76) * mm, "end": v(-9.43, 9.73) * mm});
            skLineSegment(sketch, "E375", {"start": v(-9.43, 9.73) * mm, "end": v(-9.33, 9.75) * mm});
            skLineSegment(sketch, "E376", {"start": v(-9.33, 9.75) * mm, "end": v(-9.24, 9.78) * mm});
            skLineSegment(sketch, "E377", {"start": v(-9.24, 9.78) * mm, "end": v(-8, 10.81) * mm});
            skLineSegment(sketch, "E378", {"start": v(-8, 10.81) * mm, "end": v(-7.96, 10.9) * mm});
            skLineSegment(sketch, "E379", {"start": v(-7.96, 10.9) * mm, "end": v(-7.93, 11) * mm});
            skLineSegment(sketch, "E380", {"start": v(-7.93, 11) * mm, "end": v(-7.95, 11.03) * mm});
            skLineSegment(sketch, "E381", {"start": v(-7.95, 11.03) * mm, "end": v(-8, 11.12) * mm});
            skLineSegment(sketch, "E382", {"start": v(-8, 11.12) * mm, "end": v(-8.04, 11.2) * mm});
            skLineSegment(sketch, "E383", {"start": v(-8.04, 11.2) * mm, "end": v(-8.08, 11.3) * mm});
            skLineSegment(sketch, "E384", {"start": v(-8.08, 11.3) * mm, "end": v(-8.15, 11.48) * mm});
            skLineSegment(sketch, "E385", {"start": v(-8.15, 11.48) * mm, "end": v(-8.21, 11.67) * mm});
            skLineSegment(sketch, "E386", {"start": v(-8.21, 11.67) * mm, "end": v(-8.27, 11.86) * mm});
            skLineSegment(sketch, "E387", {"start": v(-8.27, 11.86) * mm, "end": v(-8.31, 12.06) * mm});
            skLineSegment(sketch, "E388", {"start": v(-8.31, 12.06) * mm, "end": v(-8.35, 12.27) * mm});
            skLineSegment(sketch, "E389", {"start": v(-8.35, 12.27) * mm, "end": v(-8.39, 12.47) * mm});
            skLineSegment(sketch, "E390", {"start": v(-8.39, 12.47) * mm, "end": v(-8.41, 12.68) * mm});
            skLineSegment(sketch, "E391", {"start": v(-8.41, 12.68) * mm, "end": v(-8.43, 12.85) * mm});
            skLineSegment(sketch, "E392", {"start": v(-8.43, 12.85) * mm, "end": v(-6.89, 13.74) * mm});
            skLineSegment(sketch, "E393", {"start": v(-6.89, 13.74) * mm, "end": v(-6.75, 13.64) * mm});
            skLineSegment(sketch, "E394", {"start": v(-6.75, 13.64) * mm, "end": v(-6.59, 13.51) * mm});
            skLineSegment(sketch, "E395", {"start": v(-6.59, 13.51) * mm, "end": v(-6.42, 13.38) * mm});
            skLineSegment(sketch, "E396", {"start": v(-6.42, 13.38) * mm, "end": v(-6.27, 13.24) * mm});
            skLineSegment(sketch, "E397", {"start": v(-6.27, 13.24) * mm, "end": v(-6.12, 13.1) * mm});
            skLineSegment(sketch, "E398", {"start": v(-6.12, 13.1) * mm, "end": v(-5.97, 12.96) * mm});
            skLineSegment(sketch, "E399", {"start": v(-5.97, 12.96) * mm, "end": v(-5.84, 12.8) * mm});
            skLineSegment(sketch, "E400", {"start": v(-5.84, 12.8) * mm, "end": v(-5.72, 12.66) * mm});
            skLineSegment(sketch, "E401", {"start": v(-5.72, 12.66) * mm, "end": v(-5.66, 12.58) * mm});
            skLineSegment(sketch, "E402", {"start": v(-5.66, 12.58) * mm, "end": v(-5.6, 12.5) * mm});
            skLineSegment(sketch, "E403", {"start": v(-5.6, 12.5) * mm, "end": v(-5.56, 12.41) * mm});
            skLineSegment(sketch, "E404", {"start": v(-5.56, 12.41) * mm, "end": v(-5.53, 12.37) * mm});
            skLineSegment(sketch, "E405", {"start": v(-5.53, 12.37) * mm, "end": v(-5.44, 12.36) * mm});
            skLineSegment(sketch, "E406", {"start": v(-5.44, 12.36) * mm, "end": v(-5.34, 12.35) * mm});
            skLineSegment(sketch, "E407", {"start": v(-5.34, 12.35) * mm, "end": v(-3.83, 12.9) * mm});
            skLineSegment(sketch, "E408", {"start": v(-3.83, 12.9) * mm, "end": v(-3.76, 12.97) * mm});
            skLineSegment(sketch, "E409", {"start": v(-3.76, 12.97) * mm, "end": v(-3.7, 13.04) * mm});
            skLineSegment(sketch, "E410", {"start": v(-3.7, 13.04) * mm, "end": v(-3.7, 13.09) * mm});
            skLineSegment(sketch, "E411", {"start": v(-3.7, 13.09) * mm, "end": v(-3.72, 13.18) * mm});
            skLineSegment(sketch, "E412", {"start": v(-3.72, 13.18) * mm, "end": v(-3.73, 13.28) * mm});
            skLineSegment(sketch, "E413", {"start": v(-3.73, 13.28) * mm, "end": v(-3.73, 13.38) * mm});
            skLineSegment(sketch, "E414", {"start": v(-3.73, 13.38) * mm, "end": v(-3.74, 13.58) * mm});
            skLineSegment(sketch, "E415", {"start": v(-3.74, 13.58) * mm, "end": v(-3.73, 13.77) * mm});
            skLineSegment(sketch, "E416", {"start": v(-3.73, 13.77) * mm, "end": v(-3.72, 13.98) * mm});
            skLineSegment(sketch, "E417", {"start": v(-3.72, 13.98) * mm, "end": v(-3.7, 14.18) * mm});
            skLineSegment(sketch, "E418", {"start": v(-3.7, 14.18) * mm, "end": v(-3.66, 14.39) * mm});
            skLineSegment(sketch, "E419", {"start": v(-3.66, 14.39) * mm, "end": v(-3.62, 14.6) * mm});
            skLineSegment(sketch, "E420", {"start": v(-3.62, 14.6) * mm, "end": v(-3.57, 14.8) * mm});
            skLineSegment(sketch, "E421", {"start": v(-3.57, 14.8) * mm, "end": v(-3.53, 14.96) * mm});
            skLineSegment(sketch, "E422", {"start": v(-3.53, 14.96) * mm, "end": v(-1.78, 15.27) * mm});
            skLineSegment(sketch, "E423", {"start": v(-1.78, 15.27) * mm, "end": v(-1.69, 15.13) * mm});
            skLineSegment(sketch, "E424", {"start": v(-1.69, 15.13) * mm, "end": v(-1.57, 14.95) * mm});
            skLineSegment(sketch, "E425", {"start": v(-1.57, 14.95) * mm, "end": v(-1.46, 14.77) * mm});
            skLineSegment(sketch, "E426", {"start": v(-1.46, 14.77) * mm, "end": v(-1.36, 14.6) * mm});
            skLineSegment(sketch, "E427", {"start": v(-1.36, 14.6) * mm, "end": v(-1.27, 14.4) * mm});
            skLineSegment(sketch, "E428", {"start": v(-1.27, 14.4) * mm, "end": v(-1.19, 14.22) * mm});
            skLineSegment(sketch, "E429", {"start": v(-1.19, 14.22) * mm, "end": v(-1.11, 14.04) * mm});
            skLineSegment(sketch, "E430", {"start": v(-1.11, 14.04) * mm, "end": v(-1.05, 13.85) * mm});
            skLineSegment(sketch, "E431", {"start": v(-1.05, 13.85) * mm, "end": v(-1.02, 13.76) * mm});
            skLineSegment(sketch, "E432", {"start": v(-1.02, 13.76) * mm, "end": v(-1, 13.66) * mm});
            skLineSegment(sketch, "E433", {"start": v(-1, 13.66) * mm, "end": v(-0.98, 13.57) * mm});
            skLineSegment(sketch, "E434", {"start": v(-0.98, 13.57) * mm, "end": v(-0.97, 13.52) * mm});
            skLineSegment(sketch, "E435", {"start": v(-0.97, 13.52) * mm, "end": v(-0.9, 13.48) * mm});
            skLineSegment(sketch, "E436", {"start": v(-0.9, 13.48) * mm, "end": v(-0.8, 13.44) * mm});
            skLineSegment(sketch, "E437", {"start": v(-0.8, 13.44) * mm, "end": v(0.8, 13.44) * mm});
            skLineSegment(sketch, "E438", {"start": v(0.8, 13.44) * mm, "end": v(0.9, 13.48) * mm});
            skLineSegment(sketch, "E439", {"start": v(0.9, 13.48) * mm, "end": v(0.99, 13.52) * mm});
            skLineSegment(sketch, "E440", {"start": v(0.99, 13.52) * mm, "end": v(1, 13.57) * mm});
            skLineSegment(sketch, "E441", {"start": v(1, 13.57) * mm, "end": v(1.01, 13.66) * mm});
            skLineSegment(sketch, "E442", {"start": v(1.01, 13.66) * mm, "end": v(1.03, 13.76) * mm});
            skLineSegment(sketch, "E443", {"start": v(1.03, 13.76) * mm, "end": v(1.06, 13.85) * mm});
            skLineSegment(sketch, "E444", {"start": v(1.06, 13.85) * mm, "end": v(1.12, 14.04) * mm});
            skLineSegment(sketch, "E445", {"start": v(1.12, 14.04) * mm, "end": v(1.2, 14.22) * mm});
            skLineSegment(sketch, "E446", {"start": v(1.2, 14.22) * mm, "end": v(1.28, 14.4) * mm});
            skLineSegment(sketch, "E447", {"start": v(1.28, 14.4) * mm, "end": v(1.37, 14.6) * mm});
            skLineSegment(sketch, "E448", {"start": v(1.37, 14.6) * mm, "end": v(1.48, 14.77) * mm});
            skLineSegment(sketch, "E449", {"start": v(1.48, 14.77) * mm, "end": v(1.58, 14.95) * mm});
            skLineSegment(sketch, "E450", {"start": v(1.58, 14.95) * mm, "end": v(1.7, 15.13) * mm});
            skLineSegment(sketch, "E451", {"start": v(1.7, 15.13) * mm, "end": v(1.79, 15.27) * mm});
            skLineSegment(sketch, "E452", {"start": v(1.79, 15.27) * mm, "end": v(3.55, 14.96) * mm});
            skLineSegment(sketch, "E453", {"start": v(3.55, 14.96) * mm, "end": v(3.59, 14.8) * mm});
            skLineSegment(sketch, "E454", {"start": v(3.59, 14.8) * mm, "end": v(3.63, 14.6) * mm});
            skLineSegment(sketch, "E455", {"start": v(3.63, 14.6) * mm, "end": v(3.67, 14.39) * mm});
            skLineSegment(sketch, "E456", {"start": v(3.67, 14.39) * mm, "end": v(3.7, 14.18) * mm});
            skLineSegment(sketch, "E457", {"start": v(3.7, 14.18) * mm, "end": v(3.73, 13.98) * mm});
            skLineSegment(sketch, "E458", {"start": v(3.73, 13.98) * mm, "end": v(3.74, 13.77) * mm});
            skLineSegment(sketch, "E459", {"start": v(3.74, 13.77) * mm, "end": v(3.75, 13.58) * mm});
            skLineSegment(sketch, "E460", {"start": v(3.75, 13.58) * mm, "end": v(3.75, 13.38) * mm});
            skLineSegment(sketch, "E461", {"start": v(3.75, 13.38) * mm, "end": v(3.74, 13.28) * mm});
            skLineSegment(sketch, "E462", {"start": v(3.74, 13.28) * mm, "end": v(3.73, 13.18) * mm});
            skLineSegment(sketch, "E463", {"start": v(3.73, 13.18) * mm, "end": v(3.71, 13.09) * mm});
            skLineSegment(sketch, "E464", {"start": v(3.71, 13.09) * mm, "end": v(3.7, 13.04) * mm});
            skLineSegment(sketch, "E465", {"start": v(3.7, 13.04) * mm, "end": v(3.77, 12.97) * mm});
            skLineSegment(sketch, "E466", {"start": v(3.77, 12.97) * mm, "end": v(3.84, 12.9) * mm});
            skLineSegment(sketch, "E467", {"start": v(3.84, 12.9) * mm, "end": v(5.35, 12.35) * mm});
            skLineSegment(sketch, "E468", {"start": v(5.35, 12.35) * mm, "end": v(5.45, 12.36) * mm});
            skLineSegment(sketch, "E469", {"start": v(5.45, 12.36) * mm, "end": v(5.55, 12.37) * mm});
            skLineSegment(sketch, "E470", {"start": v(5.55, 12.37) * mm, "end": v(5.57, 12.41) * mm});
            skLineSegment(sketch, "E471", {"start": v(5.57, 12.41) * mm, "end": v(5.62, 12.5) * mm});
            skLineSegment(sketch, "E472", {"start": v(5.62, 12.5) * mm, "end": v(5.67, 12.58) * mm});
            skLineSegment(sketch, "E473", {"start": v(5.67, 12.58) * mm, "end": v(5.73, 12.66) * mm});
            skLineSegment(sketch, "E474", {"start": v(5.73, 12.66) * mm, "end": v(5.85, 12.8) * mm});
            skLineSegment(sketch, "E475", {"start": v(5.85, 12.8) * mm, "end": v(5.99, 12.96) * mm});
            skLineSegment(sketch, "E476", {"start": v(5.99, 12.96) * mm, "end": v(6.13, 13.1) * mm});
            skLineSegment(sketch, "E477", {"start": v(6.13, 13.1) * mm, "end": v(6.28, 13.24) * mm});
            skLineSegment(sketch, "E478", {"start": v(6.28, 13.24) * mm, "end": v(6.43, 13.38) * mm});
            skLineSegment(sketch, "E479", {"start": v(6.43, 13.38) * mm, "end": v(6.6, 13.51) * mm});
            skLineSegment(sketch, "E480", {"start": v(6.6, 13.51) * mm, "end": v(6.77, 13.64) * mm});
            skLineSegment(sketch, "E481", {"start": v(6.77, 13.64) * mm, "end": v(6.9, 13.74) * mm});
            skLineSegment(sketch, "E482", {"start": v(6.9, 13.74) * mm, "end": v(8.44, 12.85) * mm});
            skLineSegment(sketch, "E483", {"start": v(8.44, 12.85) * mm, "end": v(8.43, 12.68) * mm});
            skLineSegment(sketch, "E484", {"start": v(8.43, 12.68) * mm, "end": v(8.4, 12.47) * mm});
            skLineSegment(sketch, "E485", {"start": v(8.4, 12.47) * mm, "end": v(8.37, 12.27) * mm});
            skLineSegment(sketch, "E486", {"start": v(8.37, 12.27) * mm, "end": v(8.33, 12.06) * mm});
            skLineSegment(sketch, "E487", {"start": v(8.33, 12.06) * mm, "end": v(8.28, 11.86) * mm});
            skLineSegment(sketch, "E488", {"start": v(8.28, 11.86) * mm, "end": v(8.22, 11.67) * mm});
            skLineSegment(sketch, "E489", {"start": v(8.22, 11.67) * mm, "end": v(8.16, 11.48) * mm});
            skLineSegment(sketch, "E490", {"start": v(8.16, 11.48) * mm, "end": v(8.1, 11.3) * mm});
            skLineSegment(sketch, "E491", {"start": v(8.1, 11.3) * mm, "end": v(8.05, 11.2) * mm});
            skLineSegment(sketch, "E492", {"start": v(8.05, 11.2) * mm, "end": v(8, 11.12) * mm});
            skLineSegment(sketch, "E493", {"start": v(8, 11.12) * mm, "end": v(7.96, 11.03) * mm});
            skLineSegment(sketch, "E494", {"start": v(7.96, 11.03) * mm, "end": v(7.94, 11) * mm});
            skLineSegment(sketch, "E495", {"start": v(7.94, 11) * mm, "end": v(7.97, 10.9) * mm});
            skLineSegment(sketch, "E496", {"start": v(7.97, 10.9) * mm, "end": v(8.02, 10.81) * mm});
            skLineSegment(sketch, "E497", {"start": v(8.02, 10.81) * mm, "end": v(9.25, 9.78) * mm});
            skLineSegment(sketch, "E498", {"start": v(9.25, 9.78) * mm, "end": v(9.35, 9.75) * mm});
            skLineSegment(sketch, "E499", {"start": v(9.35, 9.75) * mm, "end": v(9.44, 9.73) * mm});
            skLineSegment(sketch, "E500", {"start": v(9.44, 9.73) * mm, "end": v(9.47, 9.76) * mm});
            skLineSegment(sketch, "E501", {"start": v(9.47, 9.76) * mm, "end": v(9.55, 9.83) * mm});
            skLineSegment(sketch, "E502", {"start": v(9.55, 9.83) * mm, "end": v(9.63, 9.88) * mm});
            skLineSegment(sketch, "E503", {"start": v(9.63, 9.88) * mm, "end": v(9.7, 9.94) * mm});
            skLineSegment(sketch, "E504", {"start": v(9.7, 9.94) * mm, "end": v(9.88, 10.04) * mm});
            skLineSegment(sketch, "E505", {"start": v(9.88, 10.04) * mm, "end": v(10.05, 10.13) * mm});
            skLineSegment(sketch, "E506", {"start": v(10.05, 10.13) * mm, "end": v(10.23, 10.22) * mm});
            skLineSegment(sketch, "E507", {"start": v(10.23, 10.22) * mm, "end": v(10.42, 10.3) * mm});
            skLineSegment(sketch, "E508", {"start": v(10.42, 10.3) * mm, "end": v(10.62, 10.38) * mm});
            skLineSegment(sketch, "E509", {"start": v(10.62, 10.38) * mm, "end": v(10.82, 10.45) * mm});
            skLineSegment(sketch, "E510", {"start": v(10.82, 10.45) * mm, "end": v(11.02, 10.5) * mm});
            skLineSegment(sketch, "E511", {"start": v(11.02, 10.5) * mm, "end": v(11.17, 10.55) * mm});
            skLineSegment(sketch, "E512", {"start": v(11.17, 10.55) * mm, "end": v(12.32, 9.19) * mm});
            skLineSegment(sketch, "E513", {"start": v(12.32, 9.19) * mm, "end": v(12.25, 9.04) * mm});
            skLineSegment(sketch, "E514", {"start": v(12.25, 9.04) * mm, "end": v(12.15, 8.85) * mm});
            skLineSegment(sketch, "E515", {"start": v(12.15, 8.85) * mm, "end": v(12.05, 8.67) * mm});
            skLineSegment(sketch, "E516", {"start": v(12.05, 8.67) * mm, "end": v(11.94, 8.49) * mm});
            skLineSegment(sketch, "E517", {"start": v(11.94, 8.49) * mm, "end": v(11.83, 8.32) * mm});
            skLineSegment(sketch, "E518", {"start": v(11.83, 8.32) * mm, "end": v(11.71, 8.15) * mm});
            skLineSegment(sketch, "E519", {"start": v(11.71, 8.15) * mm, "end": v(11.59, 8) * mm});
            skLineSegment(sketch, "E520", {"start": v(11.59, 8) * mm, "end": v(11.46, 7.85) * mm});
            skLineSegment(sketch, "E521", {"start": v(11.46, 7.85) * mm, "end": v(11.4, 7.78) * mm});
            skLineSegment(sketch, "E522", {"start": v(11.4, 7.78) * mm, "end": v(11.32, 7.71) * mm});
            skLineSegment(sketch, "E523", {"start": v(11.32, 7.71) * mm, "end": v(11.25, 7.65) * mm});
            skLineSegment(sketch, "E524", {"start": v(11.25, 7.65) * mm, "end": v(11.21, 7.62) * mm});
            skLineSegment(sketch, "E525", {"start": v(11.21, 7.62) * mm, "end": v(11.22, 7.52) * mm});
            skLineSegment(sketch, "E526", {"start": v(11.22, 7.52) * mm, "end": v(11.23, 7.42) * mm});
            skLineSegment(sketch, "E527", {"start": v(11.23, 7.42) * mm, "end": v(12.03, 6.03) * mm});
            skLineSegment(sketch, "E528", {"start": v(12.03, 6.03) * mm, "end": v(12.11, 5.97) * mm});
            skLineSegment(sketch, "E529", {"start": v(12.11, 5.97) * mm, "end": v(12.2, 5.92) * mm});
            skLineSegment(sketch, "E530", {"start": v(12.2, 5.92) * mm, "end": v(12.24, 5.94) * mm});
            skLineSegment(sketch, "E531", {"start": v(12.24, 5.94) * mm, "end": v(12.33, 5.97) * mm});
            skLineSegment(sketch, "E532", {"start": v(12.33, 5.97) * mm, "end": v(12.42, 6) * mm});
            skLineSegment(sketch, "E533", {"start": v(12.42, 6) * mm, "end": v(12.51, 6.02) * mm});
            skLineSegment(sketch, "E534", {"start": v(12.51, 6.02) * mm, "end": v(12.7, 6.06) * mm});
            skLineSegment(sketch, "E535", {"start": v(12.7, 6.06) * mm, "end": v(12.9, 6.09) * mm});
            skLineSegment(sketch, "E536", {"start": v(12.9, 6.09) * mm, "end": v(13.1, 6.1) * mm});
            skLineSegment(sketch, "E537", {"start": v(13.1, 6.1) * mm, "end": v(13.31, 6.12) * mm});
            skLineSegment(sketch, "E538", {"start": v(13.31, 6.12) * mm, "end": v(13.52, 6.12) * mm});
            skLineSegment(sketch, "E539", {"start": v(13.52, 6.12) * mm, "end": v(13.73, 6.12) * mm});
            skLineSegment(sketch, "E540", {"start": v(13.73, 6.12) * mm, "end": v(13.94, 6.1) * mm});
            skLineSegment(sketch, "E541", {"start": v(13.94, 6.1) * mm, "end": v(14.1, 6.1) * mm});
            skLineSegment(sketch, "E542", {"start": v(14.1, 6.1) * mm, "end": v(14.72, 4.42) * mm});
            skLineSegment(sketch, "E543", {"start": v(14.72, 4.42) * mm, "end": v(14.6, 4.3) * mm});
            skLineSegment(sketch, "E544", {"start": v(14.6, 4.3) * mm, "end": v(14.44, 4.16) * mm});
            skLineSegment(sketch, "E545", {"start": v(14.44, 4.16) * mm, "end": v(14.28, 4.03) * mm});
            skLineSegment(sketch, "E546", {"start": v(14.28, 4.03) * mm, "end": v(14.12, 3.9) * mm});
            skLineSegment(sketch, "E547", {"start": v(14.12, 3.9) * mm, "end": v(13.96, 3.77) * mm});
            skLineSegment(sketch, "E548", {"start": v(13.96, 3.77) * mm, "end": v(13.79, 3.66) * mm});
            skLineSegment(sketch, "E549", {"start": v(13.79, 3.66) * mm, "end": v(13.62, 3.55) * mm});
            skLineSegment(sketch, "E550", {"start": v(13.62, 3.55) * mm, "end": v(13.45, 3.46) * mm});
            skLineSegment(sketch, "E551", {"start": v(13.45, 3.46) * mm, "end": v(13.36, 3.42) * mm});
            skLineSegment(sketch, "E552", {"start": v(13.36, 3.42) * mm, "end": v(13.27, 3.38) * mm});
            skLineSegment(sketch, "E553", {"start": v(13.27, 3.38) * mm, "end": v(13.18, 3.34) * mm});
            skLineSegment(sketch, "E554", {"start": v(13.18, 3.34) * mm, "end": v(13.14, 3.33) * mm});
            skLineSegment(sketch, "E555", {"start": v(13.14, 3.33) * mm, "end": v(13.1, 3.24) * mm});
            skLineSegment(sketch, "E556", {"start": v(13.1, 3.24) * mm, "end": v(13.08, 3.14) * mm});
            skLineSegment(sketch, "E557", {"start": v(13.08, 3.14) * mm, "end": v(13.36, 1.56) * mm});
            skLineSegment(sketch, "E558", {"start": v(13.25, -2.32) * mm, "end": v(15.13, -2.65) * mm});
            skLineSegment(sketch, "E559", {"start": v(11.65, -6.7) * mm, "end": v(13.3, -7.66) * mm});
            skLineSegment(sketch, "E560", {"start": v(8.65, -10.28) * mm, "end": v(9.88, -11.75) * mm});
            skLineSegment(sketch, "E561", {"start": v(4.6, -12.62) * mm, "end": v(5.26, -14.41) * mm});
            skLineSegment(sketch, "E562", {"start": v(0, -13.43) * mm, "end": v(0, -15.34) * mm});
            skLineSegment(sketch, "E563", {"start": v(-4.6, -12.62) * mm, "end": v(-5.25, -14.41) * mm});
            skLineSegment(sketch, "E564", {"start": v(-8.64, -10.28) * mm, "end": v(-9.86, -11.75) * mm});
            skLineSegment(sketch, "E565", {"start": v(-11.64, -6.7) * mm, "end": v(-13.3, -7.66) * mm});
            skLineSegment(sketch, "E566", {"start": v(-13.24, -2.32) * mm, "end": v(-15.12, -2.65) * mm});
            skLineSegment(sketch, "E567", {"start": v(-13.24, 2.35) * mm, "end": v(-15.12, 2.68) * mm});
            skLineSegment(sketch, "E568", {"start": v(-11.64, 6.74) * mm, "end": v(-13.3, 7.7) * mm});
            skLineSegment(sketch, "E569", {"start": v(-8.64, 10.32) * mm, "end": v(-9.86, 11.78) * mm});
            skLineSegment(sketch, "E570", {"start": v(-4.6, 12.65) * mm, "end": v(-5.25, 14.45) * mm});
            skLineSegment(sketch, "E571", {"start": v(0, 13.46) * mm, "end": v(0, 15.37) * mm});
            skLineSegment(sketch, "E572", {"start": v(4.6, 12.65) * mm, "end": v(5.26, 14.45) * mm});
            skLineSegment(sketch, "E573", {"start": v(8.65, 10.32) * mm, "end": v(9.88, 11.78) * mm});
            skLineSegment(sketch, "E574", {"start": v(11.65, 6.74) * mm, "end": v(13.3, 7.7) * mm});
            skLineSegment(sketch, "E575", {"start": v(13.25, 2.35) * mm, "end": v(15.13, 2.68) * mm});
            skCircle(sketch, "E576", {"center": v(0, 0) * mm, "radius": 0 * mm});
            skLineSegment(sketch, "E577", {"start": v(-3.83, 12.9) * mm, "end": v(-3.67, 12.47) * mm});
            skLineSegment(sketch, "E578", {"start": v(-0.8, 13.44) * mm, "end": v(-0.76, 12.98) * mm});
            skLineSegment(sketch, "E579", {"start": v(-5.34, 12.35) * mm, "end": v(-5.13, 11.94) * mm});
            skSolve(sketch);
        }
        {
            var Q0;
            Q0=makeQuery(id+"F0.imprint","IMPRINT",FACE,{"disambiguationData":[TD([[makeQuery(id+"F0.imprint","IMPRINT",EDGE,{"derivedFrom":sQuery(id+"F0.wireOp",EDGE,"E2")}),1.0]])]});
            extrude(context, id + "F1", {"entities" : qUnion([Q0]), "depth" : 3 * mm});
        }
        {
            var Q0;
            Q0=makeQuery(id+"F0.imprint","IMPRINT",FACE,{"disambiguationData":[TD([[makeQuery(id+"F0.imprint","IMPRINT",EDGE,{"derivedFrom":sQuery(id+"F0.wireOp",EDGE,"E17")}),-1.0]])]});
            var Q1;
            {var subQ2=sQuery(id+"F0.wireOp",EDGE,"E0");Q1=makeQuery(id+"F0.imprint","IMPRINT",FACE,{"disambiguationData":[TD([[makeQuery(id+"F0.imprint","IMPRINT",EDGE,{"derivedFrom":subQ2}),-1.0]])]});}
            var Q2;
            Q2=makeQuery(id+"F0.imprint","IMPRINT",FACE,{"disambiguationData":[TD([[makeQuery(id+"F0.imprint","IMPRINT",EDGE,{"derivedFrom":sQuery(id+"F0.wireOp",EDGE,"E5")}),1.0]])]});
            var Q3;
            Q3=makeQuery(id+"F0.imprint","IMPRINT",FACE,{"disambiguationData":[TD([[makeQuery(id+"F0.imprint","IMPRINT",EDGE,{"derivedFrom":sQuery(id+"F0.wireOp",EDGE,"E6")}),-1.0]])]});
            var Q4;
            Q4=makeQuery(id+"F0.imprint","IMPRINT",FACE,{"disambiguationData":[TD([[makeQuery(id+"F0.imprint","IMPRINT",EDGE,{"derivedFrom":sQuery(id+"F0.wireOp",EDGE,"E8.MirrorCS")}),1.0]])]});
            var Q5;
            Q5=makeQuery(id+"F0.imprint","IMPRINT",FACE,{"disambiguationData":[TD([[makeQuery(id+"F0.imprint","IMPRINT",EDGE,{"derivedFrom":sQuery(id+"F0.wireOp",EDGE,"E8.MirrorCS")}),-1.0]])]});
            extrude(context, id + "F2", {"entities" : qUnion([Q0, Q1, Q2, Q3, Q4, Q5]), "operationType" : NewBodyOperationType.ADD, "depth" : 19 * mm});
        }
        {
            var Q0;
            {var subQ0=sQuery(id+"F0.wireOp",EDGE,"E576");var subQ1=sQuery(id+"F0.wireOp",EDGE,"E1.MirrorC");var subQ2=sQuery(id+"F0.wireOp",EDGE,"E0");var subQ3=makeQuery(id+"F0.imprint","INTERSECT",VERTEX,{"disambiguationData":[OD(0.0)],"derivedFrom":[subQ2,subQ1,subQ0]});Q0=makeQuery(id+"F0.imprint","IMPRINT",FACE,{"disambiguationData":[TD([[makeQuery(id+"F0.imprint","IMPRINT",EDGE,{"disambiguationData":[TD([[subQ3,-1.0]])],"derivedFrom":subQ1}),-1.0]])]});}
            var Q1;
            {var subQ0=sQuery(id+"F0.wireOp",EDGE,"E576");var subQ1=sQuery(id+"F0.wireOp",EDGE,"E1.MirrorC");var subQ2=sQuery(id+"F0.wireOp",EDGE,"E0");var subQ3=makeQuery(id+"F0.imprint","INTERSECT",VERTEX,{"disambiguationData":[OD(0.0)],"derivedFrom":[subQ2,subQ1,subQ0]});Q1=makeQuery(id+"F0.imprint","IMPRINT",FACE,{"disambiguationData":[TD([[makeQuery(id+"F0.imprint","IMPRINT",EDGE,{"disambiguationData":[TD([[subQ3,-1.0]])],"derivedFrom":subQ1}),1.0]])]});}
            var Q2;
            Q2=makeQuery(id+"F0.imprint","IMPRINT",FACE,{"disambiguationData":[TD([[makeQuery(id+"F0.imprint","IMPRINT",EDGE,{"derivedFrom":sQuery(id+"F0.wireOp",EDGE,"E4")}),-1.0]])]});
            var Q3;
            {var subQ0=sQuery(id+"F0.wireOp",EDGE,"E0");Q3=makeQuery(id+"F0.imprint","IMPRINT",FACE,{"disambiguationData":[TD([[makeQuery(id+"F0.imprint","IMPRINT",EDGE,{"derivedFrom":subQ0}),1.0]])]});}
            extrude(context, id + "F3", {"entities" : qUnion([Q0, Q1, Q2, Q3]), "operationType" : NewBodyOperationType.ADD, "depth" : 1.5 * mm});
        }
    });
